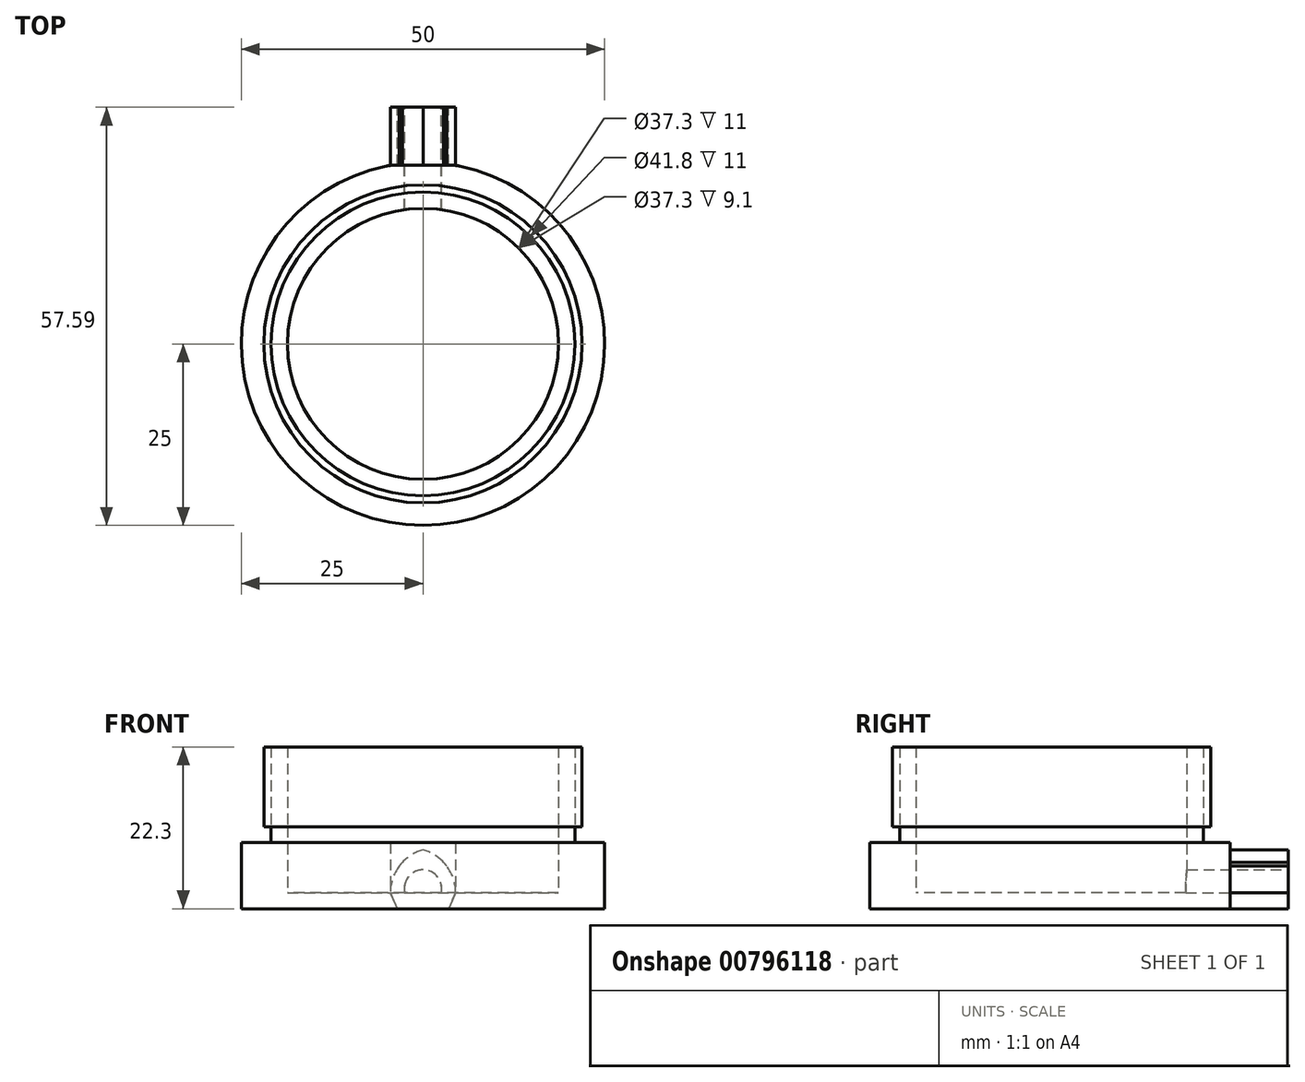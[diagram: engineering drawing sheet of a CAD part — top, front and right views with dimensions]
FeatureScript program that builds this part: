
annotation { "Feature Type Name" : "Feature", "Feature Type Description" : "" }
export const myFeature = defineFeature(function(context is Context, id is Id, definition is map)
    precondition{}
    {
        {
            var Q0;
            Q0=qCreatedBy(makeId("Top.planeOp"),FACE);
            var sketch = newSketch(context, id + "F0", { "sketchPlane" : qUnion([Q0])});
            skCircle(sketch, "E0", {"center": v(0, 0) * mm, "radius": 25 * mm});
            skPoint(sketch, "E1", {"position": v(4.5, 24.6) * mm});
            skPoint(sketch, "E2", {"position": v(-4.5, 24.6) * mm});
            skLineSegment(sketch, "E3", {"start": v(-4.5, 24.6) * mm, "end": v(-4.5, 32.6) * mm});
            skLineSegment(sketch, "E4", {"start": v(-4.5, 32.6) * mm, "end": v(4.5, 32.6) * mm});
            skLineSegment(sketch, "E5", {"start": v(4.5, 32.6) * mm, "end": v(4.5, 24.6) * mm});
            skSolve(sketch);
        }
        {
            var Q0;
            {var subQ0=sQuery(id+"F0.wireOp",EDGE,"E0");var subQ1=makeQuery(id+"F0.imprint","INTERSECT",VERTEX,{"derivedFrom":[subQ0,sQuery(id+"F0.wireOp",EDGE,"E3")]});Q0=makeQuery(id+"F0.imprint","IMPRINT",FACE,{"disambiguationData":[TD([[makeQuery(id+"F0.imprint","IMPRINT",EDGE,{"disambiguationData":[TD([[subQ1,1.0]])],"derivedFrom":subQ0}),1.0]])]});}
            var Q1;
            {var subQ0=sQuery(id+"F0.wireOp",EDGE,"E3");Q1=makeQuery(id+"F0.imprint","IMPRINT",FACE,{"disambiguationData":[TD([[makeQuery(id+"F0.imprint","IMPRINT",EDGE,{"derivedFrom":subQ0}),-1.0]])]});}
            extrude(context, id + "F1", {"entities" : qUnion([Q0, Q1]), "depth" : 2.2 * mm, "offsetDistance" : 25 * mm});
        }
        {
            var Q0;
            Q0=makeQuery(id+"F1.opExtrude","SWEPT_FACE",FACE,{"disambiguationData":[OSD([sQuery(id+"F0.wireOp",EDGE,"E4")])]});
            var sketch = newSketch(context, id + "F2", { "sketchPlane" : qUnion([Q0])});
            skLineSegment(sketch, "E6", {"start": v(-4.5, 2.2) * mm, "end": v(-3.5, 0) * mm});
            skLineSegment(sketch, "E7", {"start": v(4.5, 2.2) * mm, "end": v(3.5, 0) * mm});
            skSolve(sketch);
        }
        {
            var Q0;
            {var subQ0=sQuery(id+"F2.wireOp",EDGE,"E6");Q0=makeQuery(id+"F2.imprint","IMPRINT",FACE,{"disambiguationData":[TD([[makeQuery(id+"F2.imprint","IMPRINT",EDGE,{"derivedFrom":subQ0}),-1.0]])]});}
            var Q1;
            {var subQ0=sQuery(id+"F2.wireOp",EDGE,"E7");Q1=makeQuery(id+"F2.imprint","IMPRINT",FACE,{"disambiguationData":[TD([[makeQuery(id+"F2.imprint","IMPRINT",EDGE,{"derivedFrom":subQ0}),1.0]])]});}
            extrude(context, id + "F3", {"entities" : qUnion([Q0, Q1]), "operationType" : NewBodyOperationType.REMOVE, "oppositeDirection" : true, "depth" : 8 * mm, "offsetDistance" : 25 * mm});
        }
        {
            var Q0;
            {var subQ0=sQuery(id+"F0.wireOp",EDGE,"E3");Q0=makeQuery(id+"F3.boolean.opBoolean","MERGE",EDGE,{"derivedFrom":[makeQuery(id+"F1.opExtrude","SWEPT_EDGE",EDGE,{"disambiguationData":[OSD([sQuery(id+"F0.wireOp",EDGE,"E0"),subQ0])]}),makeQuery(id+"F3.opExtrude","CAP_EDGE",EDGE,{"disambiguationData":[OSD([subQ0,sQuery(id+"F0.wireOp",EDGE,"E4")])],"isStart":false})]});}
            var Q1;
            {var subQ0=sQuery(id+"F0.wireOp",EDGE,"E5");Q1=makeQuery(id+"F3.boolean.opBoolean","MERGE",EDGE,{"derivedFrom":[makeQuery(id+"F1.opExtrude","SWEPT_EDGE",EDGE,{"disambiguationData":[OSD([sQuery(id+"F0.wireOp",EDGE,"E0"),subQ0])]}),makeQuery(id+"F3.opExtrude","CAP_EDGE",EDGE,{"disambiguationData":[OSD([sQuery(id+"F0.wireOp",EDGE,"E4"),subQ0])],"isStart":false})]});}
            fillet(context, id + "F4", {"entities" : qUnion([Q0, Q1]), "radius" : 5 * mm, "tangentPropagation" : true, "allowEdgeOverflow" : false});
        }
        {
            var Q0;
            Q0=makeQuery(id+"F1.opExtrude","CAP_FACE",FACE,{"disambiguationData":[OSD([sQuery(id+"F0.wireOp",EDGE,"E0"),sQuery(id+"F0.wireOp",EDGE,"E3"),sQuery(id+"F0.wireOp",EDGE,"E4"),sQuery(id+"F0.wireOp",EDGE,"E5")])],"isStart":false});
            var sketch = newSketch(context, id + "F5", { "sketchPlane" : qUnion([Q0])});
            skCircle(sketch, "E8", {"center": v(0, 0) * mm, "radius": 18.65 * mm});
            skSolve(sketch);
        }
        {
            var Q0;
            Q0=makeQuery(id+"F5.imprint","IMPRINT",FACE,{"disambiguationData":[TD([[makeQuery(id+"F5.imprint","IMPRINT",EDGE,{"derivedFrom":sQuery(id+"F5.wireOp",EDGE,"E8")}),-1.0]])]});
            extrude(context, id + "F6", {"entities" : qUnion([Q0]), "operationType" : NewBodyOperationType.ADD, "depth" : 5.9 * mm, "offsetDistance" : 25 * mm});
        }
        {
            var Q0;
            {var subQ0=sQuery(id+"F0.wireOp",EDGE,"E4");Q0=makeQuery(id+"F6.boolean.opBoolean","MERGE",FACE,{"derivedFrom":[makeQuery(id+"F1.opExtrude","SWEPT_FACE",FACE,{"disambiguationData":[OSD([subQ0])]}),makeQuery(id+"F6.opExtrude","SWEPT_FACE",FACE,{"disambiguationData":[OSD([subQ0])]})]});}
            var sketch = newSketch(context, id + "F7", { "sketchPlane" : qUnion([Q0])});
            skLineSegment(sketch, "E9", {"start": v(-4.5, 2.2) * mm, "end": v(4.5, 2.2) * mm});
            skArc(sketch, "E10", {"start": v(0, 8.1) * mm, "mid": v(-3.25, 5.91) * mm, "end": v(-4.5, 2.2) * mm});
            skArc(sketch, "E11", {"start": v(4.5, 2.2) * mm, "mid": v(3.25, 5.91) * mm, "end": v(0, 8.1) * mm});
            skArc(sketch, "E12", {"start": v(3.25, 5.9) * mm, "mid": v(0, 7.57) * mm, "end": v(-3.25, 5.9) * mm});
            skSolve(sketch);
        }
        {
            var Q0;
            {var subQ0=sQuery(id+"F2.wireOp",EDGE,"E6");var subQ1=sQuery(id+"F0.wireOp",EDGE,"E4");var subQ2=makeQuery(id+"F6.opExtrude","SWEPT_EDGE",EDGE,{"disambiguationData":[OSD([subQ1,sQuery(id+"F0.wireOp",EDGE,"E5"),subQ0])]});Q0=makeQuery(id+"F7.imprint","IMPRINT",FACE,{"disambiguationData":[TD([[makeQuery(id+"F7.imprint","IMPRINT",EDGE,{"derivedFrom":subQ2}),1.0]])]});}
            var Q1;
            {var subQ0=sQuery(id+"F2.wireOp",EDGE,"E7");var subQ1=sQuery(id+"F0.wireOp",EDGE,"E4");var subQ2=makeQuery(id+"F6.opExtrude","SWEPT_EDGE",EDGE,{"disambiguationData":[OSD([sQuery(id+"F0.wireOp",EDGE,"E3"),subQ1,subQ0])]});Q1=makeQuery(id+"F7.imprint","IMPRINT",FACE,{"disambiguationData":[TD([[makeQuery(id+"F7.imprint","IMPRINT",EDGE,{"derivedFrom":subQ2}),-1.0]])]});}
            var Q2;
            {var subQ1=sQuery(id+"F7.wireOp",EDGE,"E10");var subQ3=sQuery(id+"F7.wireOp",EDGE,"bIeHIq6R-q6Z2-TFDy-dnME-hyocAYD4Mxim");var subQ4=makeQuery(id+"F7.imprint","INTERSECT",VERTEX,{"disambiguationData":[OD(1.0)],"derivedFrom":[subQ1,subQ3]});Q2=makeQuery(id+"F7.imprint","IMPRINT",FACE,{"disambiguationData":[TD([[makeQuery(id+"F7.imprint","IMPRINT",EDGE,{"disambiguationData":[TD([[subQ4,1.0]])],"derivedFrom":subQ3}),-1.0]])]});}
            extrude(context, id + "F8", {"entities" : qUnion([Q0, Q1, Q2]), "operationType" : NewBodyOperationType.REMOVE, "oppositeDirection" : true, "depth" : 8 * mm, "offsetDistance" : 25 * mm});
        }
        {
            var Q0;
            {var subQ1=sQuery(id+"F7.wireOp",EDGE,"E10");var subQ3=sQuery(id+"F7.wireOp",EDGE,"E12");var subQ4=makeQuery(id+"F7.imprint","INTERSECT",VERTEX,{"disambiguationData":[OD(1.0)],"derivedFrom":[subQ1,subQ3]});Q0=makeQuery(id+"F7.imprint","IMPRINT",FACE,{"disambiguationData":[TD([[makeQuery(id+"F7.imprint","IMPRINT",EDGE,{"disambiguationData":[TD([[subQ4,1.0]])],"derivedFrom":subQ3}),-1.0]])]});}
            extrude(context, id + "F9", {"entities" : qUnion([Q0]), "operationType" : NewBodyOperationType.REMOVE, "oppositeDirection" : true, "depth" : 8 * mm, "offsetDistance" : 25 * mm});
        }
        {
            var Q0;
            {var subQ0=sQuery(id+"F0.wireOp",EDGE,"E4");Q0=makeQuery(id+"F6.boolean.opBoolean","MERGE",FACE,{"derivedFrom":[makeQuery(id+"F1.opExtrude","SWEPT_FACE",FACE,{"disambiguationData":[OSD([subQ0])]}),makeQuery(id+"F6.opExtrude","SWEPT_FACE",FACE,{"disambiguationData":[OSD([subQ0])]})]});}
            var sketch = newSketch(context, id + "F10", { "sketchPlane" : qUnion([Q0])});
            skLineSegment(sketch, "E13", {"start": v(-4.5, 2.2) * mm, "end": v(4.5, 2.2) * mm});
            skPoint(sketch, "E14", {"position": v(-2.5, 2.2) * mm});
            skPoint(sketch, "E15", {"position": v(2.5, 2.2) * mm});
            skArc(sketch, "E16", {"start": v(2.5, 2.2) * mm, "mid": v(0, 5.37) * mm, "end": v(-2.5, 2.2) * mm});
            skSolve(sketch);
        }
        {
            var Q0;
            {var subQ0=sQuery(id+"F10.wireOp",EDGE,"E16");Q0=makeQuery(id+"F10.imprint","IMPRINT",FACE,{"disambiguationData":[TD([[makeQuery(id+"F10.imprint","IMPRINT",EDGE,{"derivedFrom":subQ0}),1.0]])]});}
            extrude(context, id + "F11", {"entities" : qUnion([Q0]), "operationType" : NewBodyOperationType.REMOVE, "oppositeDirection" : true, "depth" : 15 * mm, "offsetDistance" : 25 * mm});
        }
        {
            var Q0;
            Q0=makeQuery(id+"F6.opExtrude","CAP_FACE",FACE,{"disambiguationData":[OSD([sQuery(id+"F0.wireOp",EDGE,"E0"),sQuery(id+"F0.wireOp",EDGE,"E3"),sQuery(id+"F0.wireOp",EDGE,"E4"),sQuery(id+"F0.wireOp",EDGE,"E5"),sQuery(id+"F2.wireOp",EDGE,"E6"),sQuery(id+"F2.wireOp",EDGE,"E7"),sQuery(id+"F5.wireOp",EDGE,"E8")])],"isStart":false});
            extrude(context, id + "F12", {"entities" : qUnion([Q0]), "operationType" : NewBodyOperationType.ADD, "depth" : 1 * mm, "offsetDistance" : 25 * mm});
        }
        {
            var Q0;
            Q0=makeQuery(id+"F12.opExtrude","CAP_FACE",FACE,{"disambiguationData":[OSD([sQuery(id+"F0.wireOp",EDGE,"E0"),sQuery(id+"F0.wireOp",EDGE,"E3"),sQuery(id+"F0.wireOp",EDGE,"E4"),sQuery(id+"F0.wireOp",EDGE,"E5"),sQuery(id+"F2.wireOp",EDGE,"E6"),sQuery(id+"F2.wireOp",EDGE,"E7"),sQuery(id+"F5.wireOp",EDGE,"E8")])],"isStart":false});
            var sketch = newSketch(context, id + "F13", { "sketchPlane" : qUnion([Q0])});
            skCircle(sketch, "E17", {"center": v(0, 0) * mm, "radius": 20.9 * mm});
            skSolve(sketch);
        }
        {
            var Q0;
            Q0=makeQuery(id+"F13.imprint","IMPRINT",FACE,{"disambiguationData":[TD([[makeQuery(id+"F13.imprint","IMPRINT",EDGE,{"derivedFrom":sQuery(id+"F13.wireOp",EDGE,"E17")}),1.0]])]});
            extrude(context, id + "F14", {"entities" : qUnion([Q0]), "operationType" : NewBodyOperationType.ADD, "depth" : 2.2 * mm, "offsetDistance" : 25 * mm});
        }
        {
            var Q0;
            Q0=makeQuery(id+"F14.opExtrude","CAP_FACE",FACE,{"disambiguationData":[OSD([sQuery(id+"F5.wireOp",EDGE,"E8"),sQuery(id+"F13.wireOp",EDGE,"E17")])],"isStart":false});
            var sketch = newSketch(context, id + "F15", { "sketchPlane" : qUnion([Q0])});
            skCircle(sketch, "E18", {"center": v(0, 0) * mm, "radius": 21.9 * mm});
            skSolve(sketch);
        }
        {
            var Q0;
            Q0=makeQuery(id+"F15.imprint","IMPRINT",FACE,{"disambiguationData":[TD([[makeQuery(id+"F15.imprint","IMPRINT",EDGE,{"derivedFrom":sQuery(id+"F15.wireOp",EDGE,"E18")}),1.0]])]});
            extrude(context, id + "F16", {"entities" : qUnion([Q0]), "depth" : 11 * mm, "offsetDistance" : 25 * mm});
        }
        {
            var Q0;
            Q0=makeQuery(id+"F14.opExtrude","CAP_FACE",FACE,{"disambiguationData":[OSD([sQuery(id+"F5.wireOp",EDGE,"E8"),sQuery(id+"F13.wireOp",EDGE,"E17")])],"isStart":false});
            extrude(context, id + "F17", {"entities" : qUnion([Q0]), "depth" : 11 * mm, "offsetDistance" : 25 * mm});
        }
    });
